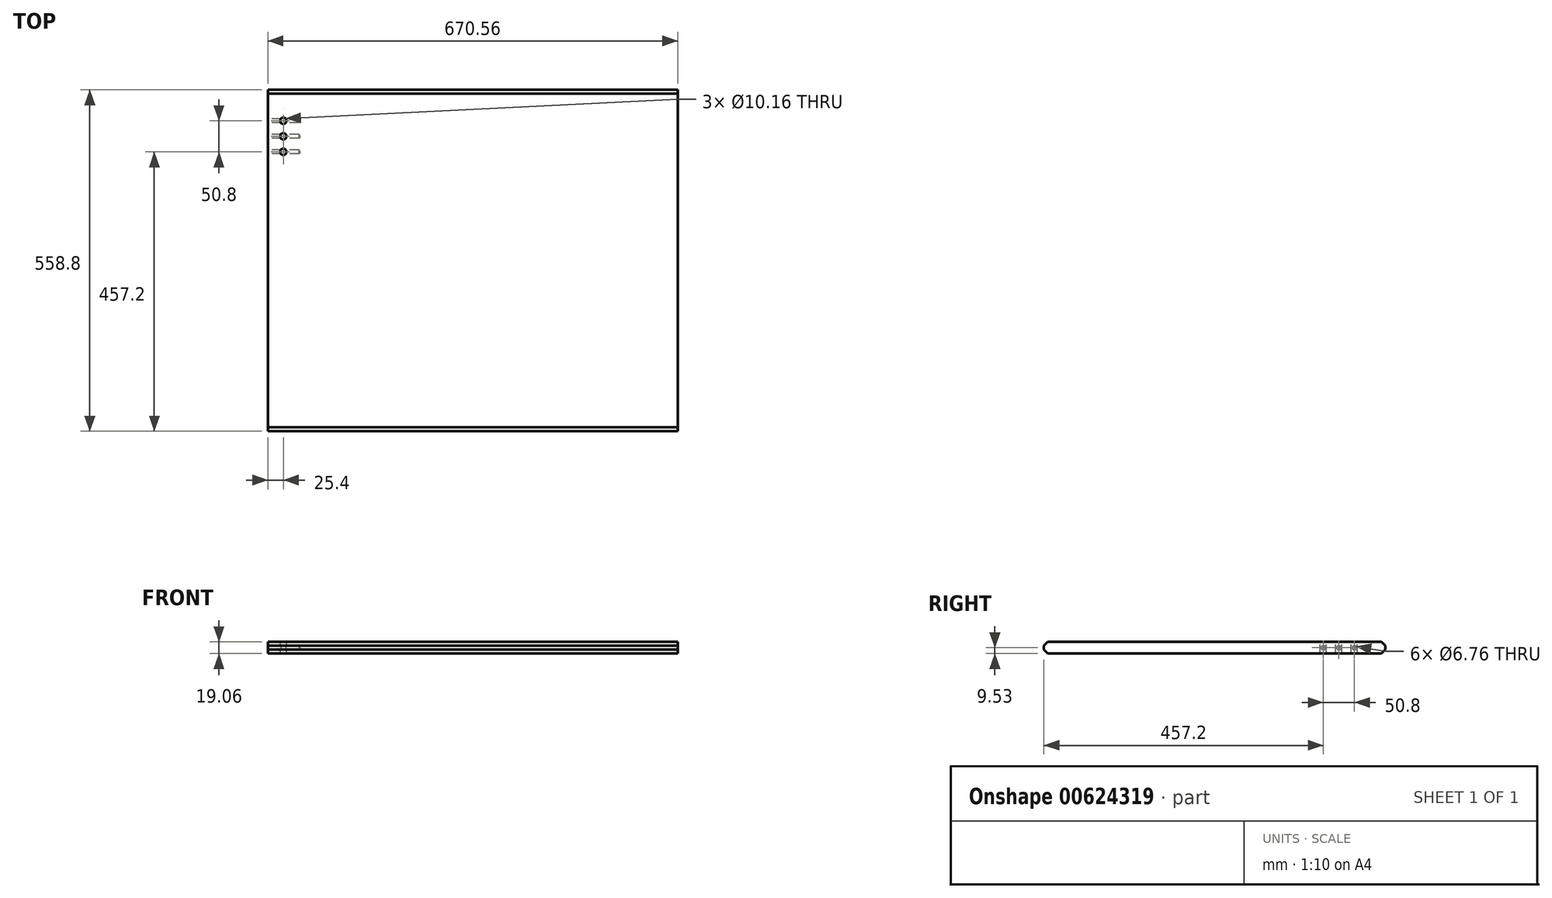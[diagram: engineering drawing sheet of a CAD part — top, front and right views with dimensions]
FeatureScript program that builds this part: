
annotation { "Feature Type Name" : "Feature", "Feature Type Description" : "" }
export const myFeature = defineFeature(function(context is Context, id is Id, definition is map)
    precondition{}
    {
        {
            var Q0;
            Q0=qCreatedBy(makeId("Top.planeOp"),FACE);
            var sketch = newSketch(context, id + "F0", { "sketchPlane" : qUnion([Q0])});
            skLineSegment(sketch, "E0.bottom", {"start": v(-335.28, -279.4) * mm, "end": v(335.28, -279.4) * mm});
            skLineSegment(sketch, "E0.top", {"start": v(-335.28, 279.4) * mm, "end": v(335.28, 279.4) * mm});
            skLineSegment(sketch, "E0.left", {"start": v(-335.28, -279.4) * mm, "end": v(-335.28, 279.4) * mm});
            skLineSegment(sketch, "E0.right", {"start": v(335.28, -279.4) * mm, "end": v(335.28, 279.4) * mm});
            skLineSegment(sketch, "E1", {"start": v(-335.28, 0) * mm, "end": v(335.28, 0) * mm, "construction": true});
            skLineSegment(sketch, "E2", {"start": v(0, 279.4) * mm, "end": v(0, -279.4) * mm, "construction": true});
            skSolve(sketch);
        }
        {
            var Q0;
            Q0=makeQuery(id+"F0.imprint","IMPRINT",FACE,{"disambiguationData":[TD([[makeQuery(id+"F0.imprint","IMPRINT",EDGE,{"derivedFrom":sQuery(id+"F0.wireOp",EDGE,"sI1gYRHP-jyey-zvMP-TBrs-d0vDupu52NdV.bottom")}),1.0]])]});
            var Q1;
            Q1=makeQuery(id+"F0.imprint","IMPRINT",FACE,{"disambiguationData":[TD([[makeQuery(id+"F0.imprint","IMPRINT",EDGE,{"derivedFrom":sQuery(id+"F0.wireOp",EDGE,"E0.bottom")}),1.0]])]});
            extrude(context, id + "F1", {"entities" : qUnion([Q0, Q1]), "endBound" : BoundingType.SYMMETRIC, "depth" : 19.05 * mm, "offsetDistance" : 25.4 * mm});
        }
        {
            var Q0;
            Q0=makeQuery(id+"F1.opExtrude","CAP_EDGE",EDGE,{"disambiguationData":[OSD([sQuery(id+"F0.wireOp",EDGE,"E0.bottom")])],"isStart":false});
            var Q1;
            Q1=makeQuery(id+"F1.opExtrude","CAP_EDGE",EDGE,{"disambiguationData":[OSD([sQuery(id+"F0.wireOp",EDGE,"E0.bottom")])],"isStart":true});
            var Q2;
            Q2=makeQuery(id+"F1.opExtrude","CAP_EDGE",EDGE,{"disambiguationData":[OSD([sQuery(id+"F0.wireOp",EDGE,"E0.top")])],"isStart":false});
            var Q3;
            Q3=makeQuery(id+"F1.opExtrude","CAP_EDGE",EDGE,{"disambiguationData":[OSD([sQuery(id+"F0.wireOp",EDGE,"E0.top")])],"isStart":true});
            chamfer(context, id + "F2", {"entities" : qUnion([Q0, Q1, Q2, Q3]), "width" : 6.35 * mm, "tangentPropagation" : true});
        }
        {
            var Q0;
            Q0=makeQuery(id+"F1.opExtrude","SWEPT_FACE",FACE,{"disambiguationData":[OSD([sQuery(id+"F0.wireOp",EDGE,"E0.left")])]});
            var sketch = newSketch(context, id + "F3", { "sketchPlane" : qUnion([Q0])});
            skPoint(sketch, "E3", {"position": v(-228.6, 0) * mm});
            skPoint(sketch, "E4", {"position": v(-203.2, 0) * mm});
            skPoint(sketch, "E5", {"position": v(-177.8, 0) * mm});
            skSolve(sketch);
        }
        {
            var Q0;
            Q0=makeQuery(id+"F1.opExtrude","CAP_FACE",FACE,{"disambiguationData":[OSD([sQuery(id+"F0.wireOp",EDGE,"E0.bottom"),sQuery(id+"F0.wireOp",EDGE,"E0.top"),sQuery(id+"F0.wireOp",EDGE,"E0.left"),sQuery(id+"F0.wireOp",EDGE,"E0.right")])],"isStart":false});
            var sketch = newSketch(context, id + "F4", { "sketchPlane" : qUnion([Q0])});
            skPoint(sketch, "E6.0", {"position": v(-335.28, 228.6) * mm});
            skPoint(sketch, "E7.0", {"position": v(-335.28, 203.2) * mm});
            skPoint(sketch, "E8.0", {"position": v(-335.28, 177.8) * mm});
            skPoint(sketch, "E9", {"position": v(-309.88, 203.2) * mm});
            skPoint(sketch, "E10", {"position": v(-309.88, 177.8) * mm});
            skPoint(sketch, "E11", {"position": v(-309.88, 228.6) * mm});
            skSolve(sketch);
        }
        {
            var Q0;
            Q0=sQuery(id+"F3.wireOp",VERTEX,"E3");
            var Q1;
            Q1=sQuery(id+"F3.wireOp",VERTEX,"E4");
            var Q2;
            Q2=sQuery(id+"F3.wireOp",VERTEX,"E5");
            var Q3;
            Q3=makeQuery(id+"F1.opExtrude","SWEPT_BODY",BODY,{"disambiguationData":[OSD([sQuery(id+"F0.wireOp",EDGE,"E0.bottom"),sQuery(id+"F0.wireOp",EDGE,"E0.top"),sQuery(id+"F0.wireOp",EDGE,"E0.left"),sQuery(id+"F0.wireOp",EDGE,"E0.right")])]});
            hole(context, id + "F5", {"style" : HoleStyle.SIMPLE, "endStyle" : HoleEndStyle.BLIND, "standardTappedOrClearance" : lookupTablePath({ "standard" : "ANSI", "fit" : "Normal (ASME)", "size" : "1/4", "type" : "Clearance" }), "standardBlindInLast" : lookupTablePath({ "fit" : "Free", "standard" : "ANSI", "size" : "1/4", "type" : "Clearance" }), "holeDiameter" : 6.76 * mm, "majorDiameter" : 6.35 * mm, "holeDepth" : 50.8 * mm, "isTappedThrough" : true, "tappedDepth" : 12.7 * mm, "tapClearance" : 3, "startFromSketch" : true, "locations" : qUnion([Q0, Q1, Q2]), "scope" : qUnion([Q3])});
        }
        {
            var Q0;
            Q0=sQuery(id+"F4.wireOp",VERTEX,"E11");
            var Q1;
            Q1=sQuery(id+"F4.wireOp",VERTEX,"E9");
            var Q2;
            Q2=sQuery(id+"F4.wireOp",VERTEX,"E10");
            var Q3;
            Q3=makeQuery(id+"F1.opExtrude","SWEPT_BODY",BODY,{"disambiguationData":[OSD([sQuery(id+"F0.wireOp",EDGE,"E0.bottom"),sQuery(id+"F0.wireOp",EDGE,"E0.top"),sQuery(id+"F0.wireOp",EDGE,"E0.left"),sQuery(id+"F0.wireOp",EDGE,"E0.right")])]});
            hole(context, id + "F6", {"style" : HoleStyle.SIMPLE, "endStyle" : HoleEndStyle.BLIND, "holeDiameter" : 10.16 * mm, "majorDiameter" : 6.35 * mm, "holeDepth" : 50.8 * mm, "isTappedThrough" : true, "tappedDepth" : 12.7 * mm, "tapClearance" : 3, "startFromSketch" : true, "locations" : qUnion([Q0, Q1, Q2]), "scope" : qUnion([Q3])});
        }
    });
